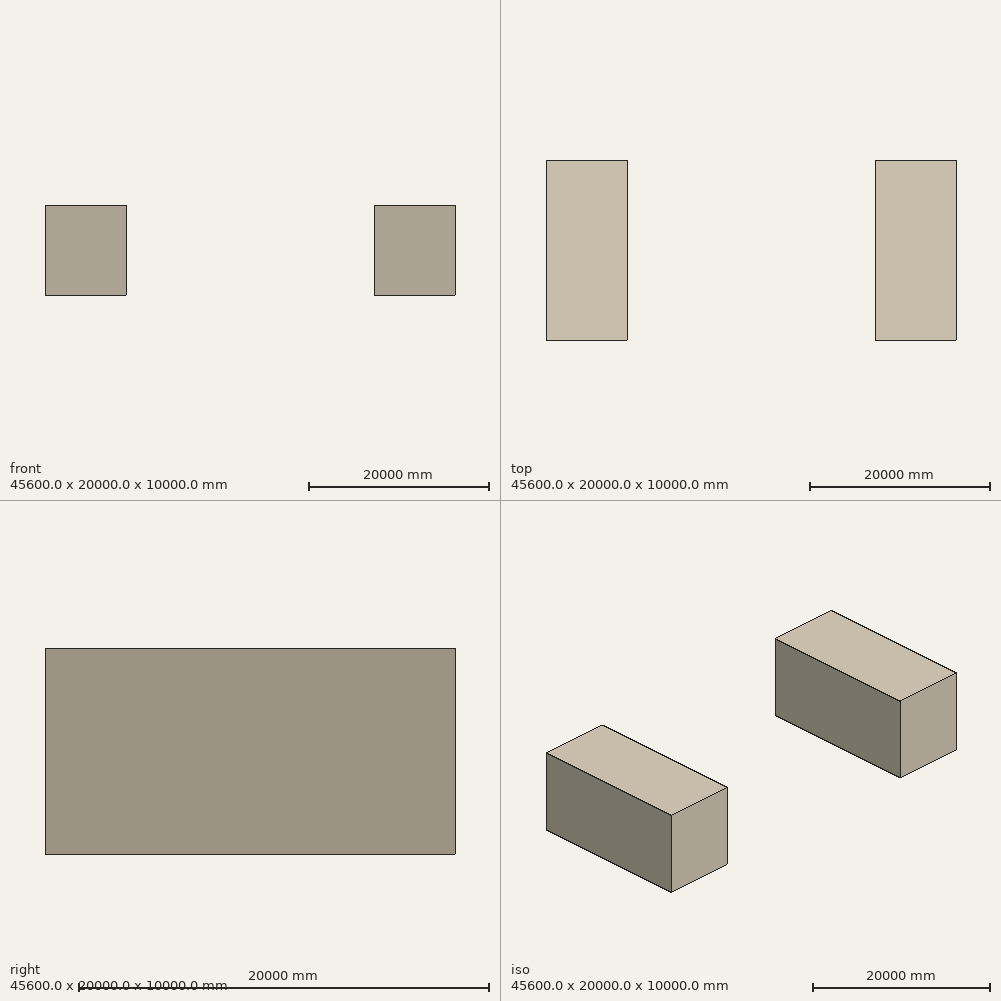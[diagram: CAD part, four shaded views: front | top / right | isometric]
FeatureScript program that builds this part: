
annotation { "Feature Type Name" : "Feature", "Feature Type Description" : "" }
export const myFeature = defineFeature(function(context is Context, id is Id, definition is map)
    precondition{}
    {
        {
            var Q0;
            Q0=qCreatedBy(makeId("Top.planeOp"),FACE);
            var sketch = newSketch(context, id + "F0", { "sketchPlane" : qUnion([Q0])});
            skLineSegment(sketch, "E0.bottom", {"start": v(-4539.44, 17467.06) * mm, "end": v(4460.56, 17467.06) * mm});
            skLineSegment(sketch, "E0.top", {"start": v(-4539.44, -2532.94) * mm, "end": v(4460.56, -2532.94) * mm});
            skLineSegment(sketch, "E0.left", {"start": v(-4539.44, 17467.06) * mm, "end": v(-4539.44, -2532.94) * mm});
            skLineSegment(sketch, "E0.right", {"start": v(4460.56, 17467.06) * mm, "end": v(4460.56, -2532.94) * mm});
            skLineSegment(sketch, "E1.bottom", {"start": v(32060.56, 17467.06) * mm, "end": v(41060.56, 17467.06) * mm});
            skLineSegment(sketch, "E1.top", {"start": v(32060.56, -2532.94) * mm, "end": v(41060.56, -2532.94) * mm});
            skLineSegment(sketch, "E1.left", {"start": v(32060.56, 17467.06) * mm, "end": v(32060.56, -2532.94) * mm});
            skLineSegment(sketch, "E1.right", {"start": v(41060.56, 17467.06) * mm, "end": v(41060.56, -2532.94) * mm});
            skSolve(sketch);
        }
        {
            var Q0;
            Q0=makeQuery(id+"F0.imprint","IMPRINT",FACE,{"disambiguationData":[TD([[makeQuery(id+"F0.imprint","IMPRINT",EDGE,{"derivedFrom":sQuery(id+"F0.wireOp",EDGE,"E0.bottom")}),-1.0]])]});
            var Q1;
            Q1=makeQuery(id+"F0.imprint","IMPRINT",FACE,{"disambiguationData":[TD([[makeQuery(id+"F0.imprint","IMPRINT",EDGE,{"derivedFrom":sQuery(id+"F0.wireOp",EDGE,"E1.bottom")}),-1.0]])]});
            extrude(context, id + "F1", {"entities" : qUnion([Q0, Q1]), "depth" : 10000 * mm});
        }
    });
